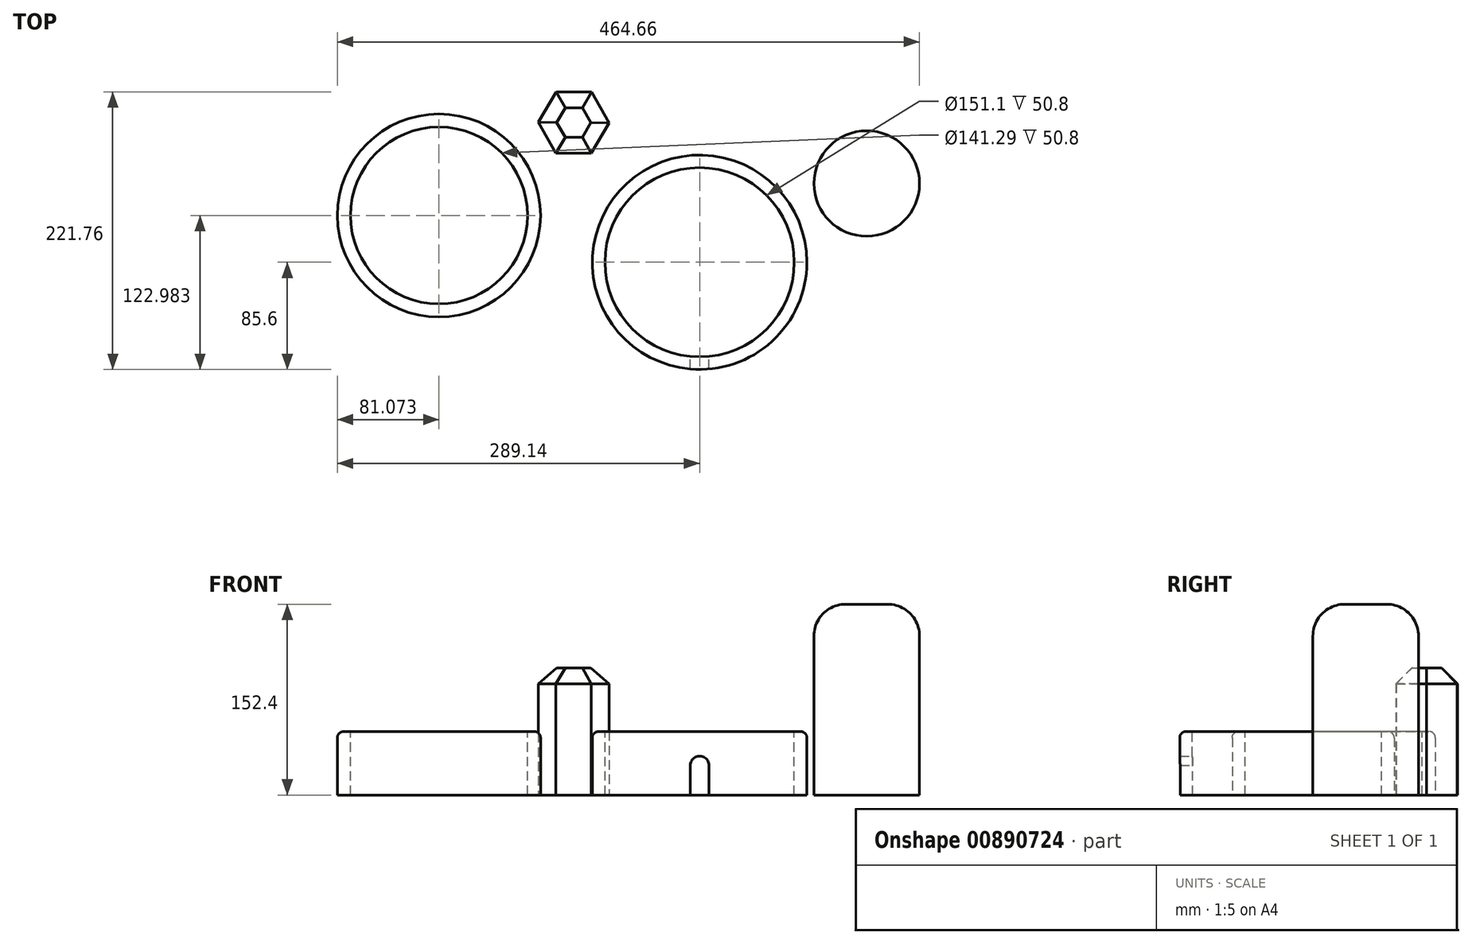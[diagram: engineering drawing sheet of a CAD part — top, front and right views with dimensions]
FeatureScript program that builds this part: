
annotation { "Feature Type Name" : "Feature", "Feature Type Description" : "" }
export const myFeature = defineFeature(function(context is Context, id is Id, definition is map)
    precondition{}
    {
        {
            var Q0;
            Q0=qCreatedBy(makeId("Top.planeOp"),FACE);
            var sketch = newSketch(context, id + "F0", { "sketchPlane" : qUnion([Q0])});
            skCircle(sketch, "E0", {"center": v(0, 0) * mm, "radius": 85.6 * mm});
            skSolve(sketch);
        }
        {
            var Q0;
            Q0=makeQuery(id+"F0.imprint","IMPRINT",FACE,{"disambiguationData":[TD([[makeQuery(id+"F0.imprint","IMPRINT",EDGE,{"derivedFrom":sQuery(id+"F0.wireOp",EDGE,"E0")}),1.0]])]});
            extrude(context, id + "F1", {"entities" : qUnion([Q0]), "depth" : 50.8 * mm, "offsetDistance" : 25.4 * mm});
        }
        {
            var Q0;
            Q0=makeQuery(id+"F1.opExtrude","CAP_EDGE",EDGE,{"disambiguationData":[OSD([sQuery(id+"F0.wireOp",EDGE,"E0")])],"isStart":false});
            fillet(context, id + "F2", {"entities" : qUnion([Q0]), "radius" : 5.08 * mm, "tangentPropagation" : true, "allowEdgeOverflow" : false});
        }
        {
            var Q0;
            Q0=makeQuery(id+"F1.opExtrude","CAP_FACE",FACE,{"disambiguationData":[OSD([sQuery(id+"F0.wireOp",EDGE,"E0")])],"isStart":false});
            var sketch = newSketch(context, id + "F3", { "sketchPlane" : qUnion([Q0])});
            skCircle(sketch, "E1", {"center": v(0, 0) * mm, "radius": 75.55 * mm});
            skSolve(sketch);
        }
        {
            var Q0;
            Q0=makeQuery(id+"F3.imprint","IMPRINT",FACE,{"disambiguationData":[TD([[makeQuery(id+"F3.imprint","IMPRINT",EDGE,{"derivedFrom":sQuery(id+"F3.wireOp",EDGE,"E1")}),1.0]])]});
            extrude(context, id + "F4", {"entities" : qUnion([Q0]), "operationType" : NewBodyOperationType.REMOVE, "oppositeDirection" : true, "depth" : 50.8 * mm, "offsetDistance" : 25.4 * mm});
        }
        {
            var Q0;
            Q0=qCreatedBy(makeId("Front.planeOp"),FACE);
            var sketch = newSketch(context, id + "F5", { "sketchPlane" : qUnion([Q0])});
            skLineSegment(sketch, "E2.bottom", {"start": v(-7.5, 0) * mm, "end": v(7.5, 0) * mm});
            skLineSegment(sketch, "E2.top", {"start": v(-7.5, 23.63) * mm, "end": v(7.5, 23.63) * mm});
            skLineSegment(sketch, "E2.left", {"start": v(-7.5, 0) * mm, "end": v(-7.5, 23.63) * mm});
            skLineSegment(sketch, "E2.right", {"start": v(7.5, 0) * mm, "end": v(7.5, 23.63) * mm});
            skPoint(sketch, "E2.middle", {"position": v(0, 11.81) * mm});
            skCircle(sketch, "E3", {"center": v(0, 23.63) * mm, "radius": 7.44 * mm});
            skSolve(sketch);
        }
        {
            var Q0;
            Q0 = qSketchRegion(id + "F5", true);
            extrude(context, id + "F6", {"entities" : qUnion([Q0]), "operationType" : NewBodyOperationType.REMOVE, "depth" : 101.6 * mm, "offsetDistance" : 25.4 * mm});
        }
        {
            var Q0;
            Q0=qCreatedBy(makeId("Top.planeOp"),FACE);
            var sketch = newSketch(context, id + "F7", { "sketchPlane" : qUnion([Q0])});
            skCircle(sketch, "E4", {"center": v(133.37, 62.88) * mm, "radius": 42.15 * mm});
            skSolve(sketch);
        }
        {
            var Q0;
            Q0=makeQuery(id+"F7.imprint","IMPRINT",FACE,{"disambiguationData":[TD([[makeQuery(id+"F7.imprint","IMPRINT",EDGE,{"derivedFrom":sQuery(id+"F7.wireOp",EDGE,"E4")}),1.0]])]});
            extrude(context, id + "F8", {"entities" : qUnion([Q0]), "depth" : 152.4 * mm, "offsetDistance" : 25.4 * mm});
        }
        {
            var Q0;
            Q0=makeQuery(id+"F8.opExtrude","CAP_EDGE",EDGE,{"disambiguationData":[OSD([sQuery(id+"F7.wireOp",EDGE,"E4")])],"isStart":false});
            fillet(context, id + "F9", {"entities" : qUnion([Q0]), "radius" : 25.4 * mm, "tangentPropagation" : true, "allowEdgeOverflow" : false});
        }
        {
            var Q0;
            Q0=qCreatedBy(makeId("Top.planeOp"),FACE);
            var sketch = newSketch(context, id + "F10", { "sketchPlane" : qUnion([Q0])});
            skCircle(sketch, "E5", {"center": v(-208.07, 37.38) * mm, "radius": 81.07 * mm});
            skSolve(sketch);
        }
        {
            var Q0;
            Q0=makeQuery(id+"F10.imprint","IMPRINT",FACE,{"disambiguationData":[TD([[makeQuery(id+"F10.imprint","IMPRINT",EDGE,{"derivedFrom":sQuery(id+"F10.wireOp",EDGE,"E5")}),1.0]])]});
            extrude(context, id + "F11", {"entities" : qUnion([Q0]), "depth" : 50.8 * mm, "offsetDistance" : 25.4 * mm});
        }
        {
            var Q0;
            Q0=makeQuery(id+"F11.opExtrude","CAP_EDGE",EDGE,{"disambiguationData":[OSD([sQuery(id+"F10.wireOp",EDGE,"E5")])],"isStart":false});
            fillet(context, id + "F12", {"entities" : qUnion([Q0]), "radius" : 5.08 * mm, "tangentPropagation" : true, "allowEdgeOverflow" : false});
        }
        {
            var Q0;
            Q0=makeQuery(id+"F11.opExtrude","CAP_FACE",FACE,{"disambiguationData":[OSD([sQuery(id+"F10.wireOp",EDGE,"E5")])],"isStart":false});
            var sketch = newSketch(context, id + "F13", { "sketchPlane" : qUnion([Q0])});
            skCircle(sketch, "E6", {"center": v(-208.07, 37.38) * mm, "radius": 70.64 * mm});
            skSolve(sketch);
        }
        {
            var Q0;
            Q0=makeQuery(id+"F13.imprint","IMPRINT",FACE,{"disambiguationData":[TD([[makeQuery(id+"F13.imprint","IMPRINT",EDGE,{"derivedFrom":sQuery(id+"F13.wireOp",EDGE,"E6")}),1.0]])]});
            extrude(context, id + "F14", {"entities" : qUnion([Q0]), "operationType" : NewBodyOperationType.REMOVE, "oppositeDirection" : true, "depth" : 50.8 * mm, "offsetDistance" : 25.4 * mm});
        }
        {
            var Q0;
            Q0=qCreatedBy(makeId("Top.planeOp"),FACE);
            var sketch = newSketch(context, id + "F15", { "sketchPlane" : qUnion([Q0])});
            skCircle(sketch, "E7.cCircle", {"center": v(-100.39, 111.58) * mm, "radius": 24.5 * mm, "construction": true});
            skLineSegment(sketch, "E7.0", {"start": v(-128.68, 111.75) * mm, "end": v(-114.39, 136.16) * mm});
            skLineSegment(sketch, "E7.1", {"start": v(-114.39, 136.16) * mm, "end": v(-86.1, 136) * mm});
            skLineSegment(sketch, "E7.2", {"start": v(-86.1, 136) * mm, "end": v(-72.1, 111.4) * mm});
            skLineSegment(sketch, "E7.3", {"start": v(-72.1, 111.4) * mm, "end": v(-86.39, 87) * mm});
            skLineSegment(sketch, "E7.4", {"start": v(-86.39, 87) * mm, "end": v(-114.68, 87.16) * mm});
            skLineSegment(sketch, "E7.5", {"start": v(-114.68, 87.16) * mm, "end": v(-128.68, 111.75) * mm});
            skPoint(sketch, "E7.0.midPoint", {"position": v(-121.53, 123.96) * mm});
            skSolve(sketch);
        }
        {
            var Q0;
            Q0=makeQuery(id+"F15.imprint","IMPRINT",FACE,{"disambiguationData":[TD([[makeQuery(id+"F15.imprint","IMPRINT",EDGE,{"derivedFrom":sQuery(id+"F15.wireOp",EDGE,"E7.0")}),-1.0]])]});
            extrude(context, id + "F16", {"entities" : qUnion([Q0]), "depth" : 101.6 * mm, "offsetDistance" : 25.4 * mm});
        }
        {
            var Q0;
            Q0=makeQuery(id+"F16.opExtrude","CAP_FACE",FACE,{"disambiguationData":[OSD([sQuery(id+"F15.wireOp",EDGE,"E7.0"),sQuery(id+"F15.wireOp",EDGE,"E7.1"),sQuery(id+"F15.wireOp",EDGE,"E7.2"),sQuery(id+"F15.wireOp",EDGE,"E7.3"),sQuery(id+"F15.wireOp",EDGE,"E7.4"),sQuery(id+"F15.wireOp",EDGE,"E7.5")])],"isStart":false});
            chamfer(context, id + "F17", {"entities" : qUnion([Q0]), "width" : 12.7 * mm, "tangentPropagation" : true});
        }
    });
